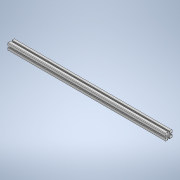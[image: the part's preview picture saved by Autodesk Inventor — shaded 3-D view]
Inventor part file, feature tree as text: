
AUTODESK INVENTOR PART (.ipt)
format: ipt  version: 2020.2 (Build 242310000, 310)  size: 176,640 bytes
history: native  units: in
note: dims shown in document units (in); Inventor stores cm internally (conversion verified against a paired STEP export)
features: extrude x1, sketch x1
ambient origin geometry x8: Origin, YZ Plane, XZ Plane, XY Plane, X Axis, Y Axis, Z Axis, Center Point
bodies: Solid1 (feature_tree)
feature tree (2):
  extrude  "Extrusion1"  Depth=0.29in
  sketch  "Sketch2"  dims[d9=0.2325in d18=0.055in d20=0.055in d34=0.29in d35=0.055in d37=0.058in d38=0.1225in d39=0.081in d40=135.0deg d41=0.17in d42=0.081in d43=0.058in d44=0.055in d45=0.75in d46=0.055in d47=1.5748in d49=360.0deg d51=0.2348in d52=0.232in d56=0.75in d58=0.125in d61=0.055in d62=0.055in d63=0.055in d64=0.055in d65=1.5748in d67=360.0deg d69=17.0in d70=0.0in d71=0.1225in]
